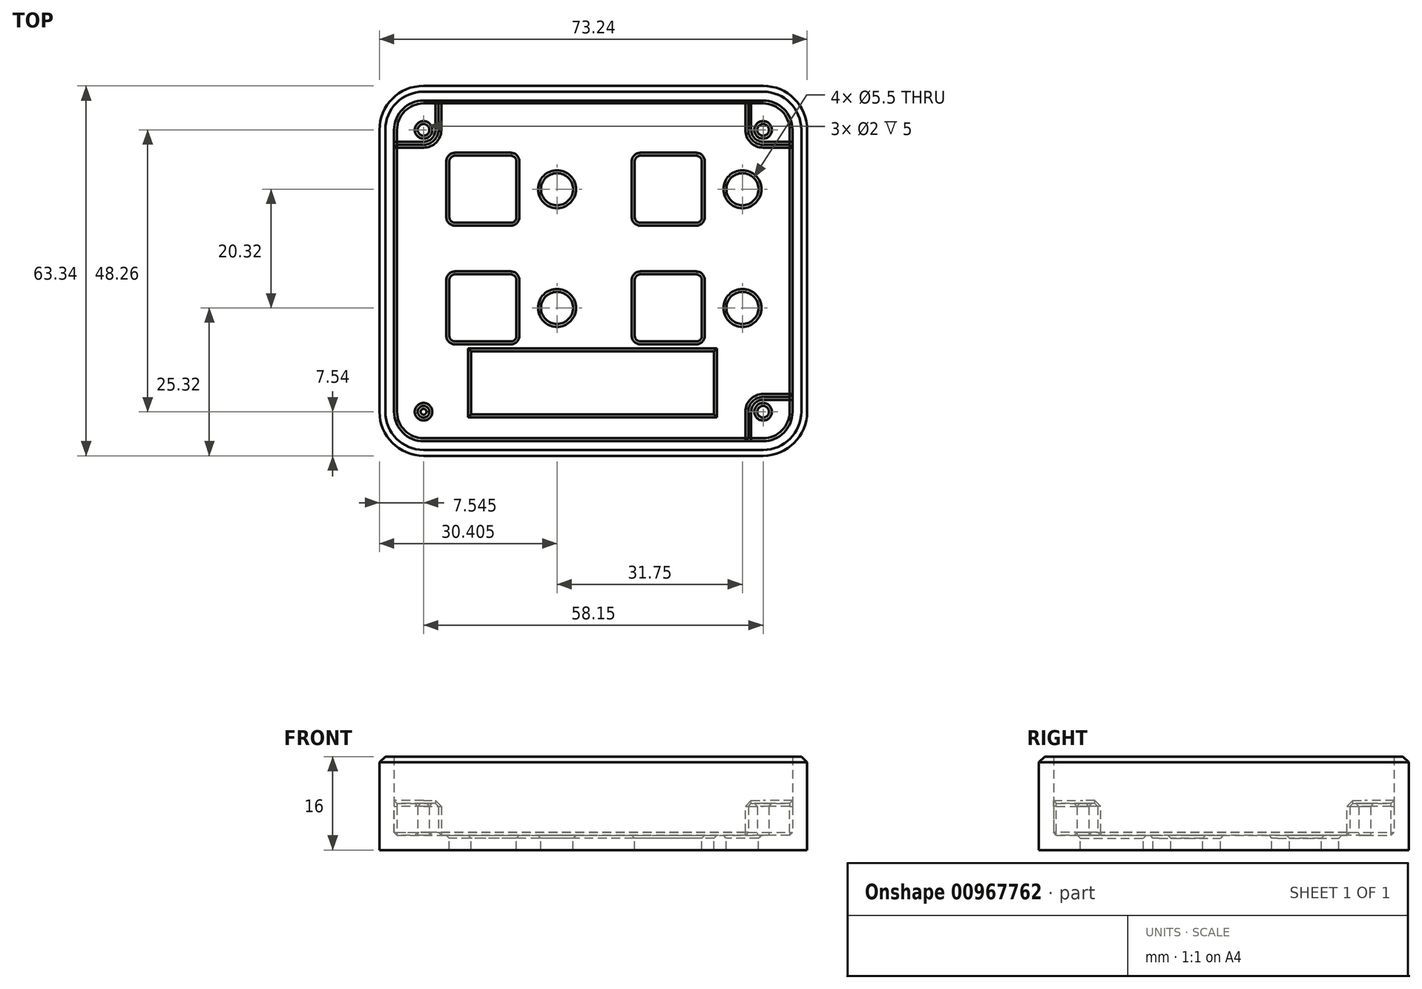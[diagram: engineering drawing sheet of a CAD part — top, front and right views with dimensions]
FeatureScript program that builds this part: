
annotation { "Feature Type Name" : "Feature", "Feature Type Description" : "" }
export const myFeature = defineFeature(function(context is Context, id is Id, definition is map)
    precondition{}
    {
        {
            var Q0;
            Q0=qCreatedBy(makeId("Top.planeOp"),FACE);
            var sketch = newSketch(context, id + "F0", { "sketchPlane" : qUnion([Q0])});
            skLineSegment(sketch, "E0.bottom", {"start": v(36.62, 31.67) * mm, "end": v(-36.61, 31.67) * mm});
            skLineSegment(sketch, "E0.top", {"start": v(36.62, -31.67) * mm, "end": v(-36.62, -31.67) * mm});
            skLineSegment(sketch, "E0.left", {"start": v(36.62, 31.67) * mm, "end": v(36.62, -31.67) * mm});
            skLineSegment(sketch, "E0.right", {"start": v(-36.62, 31.67) * mm, "end": v(-36.62, -31.67) * mm});
            skPoint(sketch, "E0.middle", {"position": v(0, 0) * mm});
            skSolve(sketch);
        }
        {
            var Q0;
            Q0 = qSketchRegion(id + "F0", true);
            extrude(context, id + "F1", {"entities" : qUnion([Q0]), "depth" : 16 * mm, "offsetDistance" : 25 * mm});
        }
        {
            var Q0;
            Q0=makeQuery(id+"F1.opExtrude","SWEPT_EDGE",EDGE,{"disambiguationData":[OSD([sQuery(id+"F0.wireOp",EDGE,"E0.top"),sQuery(id+"F0.wireOp",EDGE,"E0.right")])]});
            var Q1;
            Q1=makeQuery(id+"F1.opExtrude","SWEPT_EDGE",EDGE,{"disambiguationData":[OSD([sQuery(id+"F0.wireOp",EDGE,"E0.top"),sQuery(id+"F0.wireOp",EDGE,"E0.left")])]});
            var Q2;
            Q2=makeQuery(id+"F1.opExtrude","SWEPT_EDGE",EDGE,{"disambiguationData":[OSD([sQuery(id+"F0.wireOp",EDGE,"E0.bottom"),sQuery(id+"F0.wireOp",EDGE,"E0.left")])]});
            var Q3;
            Q3=makeQuery(id+"F1.opExtrude","SWEPT_EDGE",EDGE,{"disambiguationData":[OSD([sQuery(id+"F0.wireOp",EDGE,"E0.bottom"),sQuery(id+"F0.wireOp",EDGE,"E0.right")])]});
            fillet(context, id + "F2", {"entities" : qUnion([Q0, Q1, Q2, Q3]), "radius" : 7.54 * mm, "tangentPropagation" : true, "allowEdgeOverflow" : false});
        }
        {
            var Q0;
            Q0=makeQuery(id+"F1.opExtrude","CAP_FACE",FACE,{"disambiguationData":[OSD([sQuery(id+"F0.wireOp",EDGE,"E0.bottom"),sQuery(id+"F0.wireOp",EDGE,"E0.top"),sQuery(id+"F0.wireOp",EDGE,"E0.left"),sQuery(id+"F0.wireOp",EDGE,"E0.right")])],"isStart":false});
            shell(context, id + "F3", {"entities" : qUnion([Q0]), "thickness" : 2.5 * mm});
        }
        {
            var Q0;
            Q0=makeQuery(id+"F3.opShell","OFFSET_FACE",FACE,{"disambiguationData":[OSD([sQuery(id+"F0.wireOp",EDGE,"E0.bottom"),sQuery(id+"F0.wireOp",EDGE,"E0.top"),sQuery(id+"F0.wireOp",EDGE,"E0.left"),sQuery(id+"F0.wireOp",EDGE,"E0.right")])]});
            var sketch = newSketch(context, id + "F4", { "sketchPlane" : qUnion([Q0])});
            skLineSegment(sketch, "E1", {"start": v(-26.54, 29.17) * mm, "end": v(-26.54, 24.13) * mm});
            skLineSegment(sketch, "E2", {"start": v(-29.08, 21.6) * mm, "end": v(-34.12, 21.6) * mm});
            skCircle(sketch, "E3", {"center": v(-29.08, 24.13) * mm, "radius": 1 * mm});
            skPoint(sketch, "E4.visualSharp", {"position": v(-26.54, 21.6) * mm});
            skArc(sketch, "E4.filletArc", {"start": v(-29.08, 21.6) * mm, "mid": v(-27.28, 22.33) * mm, "end": v(-26.54, 24.13) * mm});
            skLineSegment(sketch, "E5", {"start": v(0, 29.17) * mm, "end": v(0, -29.17) * mm, "construction": true});
            skLineSegment(sketch, "E6", {"start": v(-34.12, 0) * mm, "end": v(34.12, 0) * mm, "construction": true});
            skLineSegment(sketch, "E7.MirrorCS", {"start": v(26.54, 29.17) * mm, "end": v(26.54, 24.13) * mm});
            skLineSegment(sketch, "E8.MirrorCS", {"start": v(29.08, 21.59) * mm, "end": v(34.12, 21.59) * mm});
            skArc(sketch, "E9.MirrorCS", {"start": v(29.08, 21.6) * mm, "mid": v(27.28, 22.33) * mm, "end": v(26.54, 24.13) * mm});
            skCircle(sketch, "E10.MirrorC", {"center": v(29.08, 24.13) * mm, "radius": 1 * mm});
            skCircle(sketch, "E11.MirrorC", {"center": v(-29.08, -24.13) * mm, "radius": 1 * mm});
            skCircle(sketch, "E12.MirrorC", {"center": v(29.07, -24.13) * mm, "radius": 1 * mm});
            skArc(sketch, "E13.MirrorCS", {"start": v(-29.08, -21.59) * mm, "mid": v(-27.28, -22.33) * mm, "end": v(-26.54, -24.13) * mm});
            skLineSegment(sketch, "E14.MirrorCS", {"start": v(-29.08, -21.59) * mm, "end": v(-34.12, -21.59) * mm});
            skLineSegment(sketch, "E15.MirrorCS", {"start": v(26.54, -29.17) * mm, "end": v(26.54, -24.13) * mm});
            skPoint(sketch, "E16.MirrorP", {"position": v(-26.54, -21.59) * mm});
            skLineSegment(sketch, "E17.MirrorCS", {"start": v(-26.54, -29.17) * mm, "end": v(-26.54, -24.13) * mm});
            skLineSegment(sketch, "E18.MirrorCS", {"start": v(29.07, -21.59) * mm, "end": v(34.11, -21.59) * mm});
            skArc(sketch, "E19.MirrorCS", {"start": v(29.07, -21.59) * mm, "mid": v(27.28, -22.33) * mm, "end": v(26.54, -24.13) * mm});
            skSolve(sketch);
        }
        {
            var Q0;
            {var subQ7=sQuery(id+"F4.wireOp",EDGE,"E1");Q0=makeQuery(id+"F4.imprint","IMPRINT",FACE,{"disambiguationData":[TD([[makeQuery(id+"F4.imprint","IMPRINT",EDGE,{"derivedFrom":subQ7}),-1.0]])]});}
            var Q1;
            {var subQ6=sQuery(id+"F4.wireOp",EDGE,"E7.MirrorCS");Q1=makeQuery(id+"F4.imprint","IMPRINT",FACE,{"disambiguationData":[TD([[makeQuery(id+"F4.imprint","IMPRINT",EDGE,{"derivedFrom":subQ6}),1.0]])]});}
            var Q2;
            Q2=makeQuery(id+"F4.imprint","IMPRINT",FACE,{"disambiguationData":[TD([[makeQuery(id+"F4.imprint","IMPRINT",EDGE,{"derivedFrom":sQuery(id+"F4.wireOp",EDGE,"E12.MirrorC")}),-1.0]])]});
            var Q3;
            Q3=makeQuery(id+"F4.imprint","IMPRINT",FACE,{"disambiguationData":[TD([[makeQuery(id+"F4.imprint","IMPRINT",EDGE,{"derivedFrom":sQuery(id+"F4.wireOp",EDGE,"E11.MirrorC")}),1.0]])]});
            extrude(context, id + "F5", {"entities" : qUnion([Q0, Q1, Q2, Q3]), "operationType" : NewBodyOperationType.ADD, "depth" : 5.5 * mm, "offsetDistance" : 25 * mm});
        }
        {
            var Q0;
            {var subQ0=sQuery(id+"F0.wireOp",EDGE,"E0.bottom");var subQ1=sQuery(id+"F0.wireOp",EDGE,"E0.right");var subQ2=sQuery(id+"F0.wireOp",EDGE,"E0.top");var subQ3=sQuery(id+"F0.wireOp",EDGE,"E0.left");Q0=makeQuery(id+"F5.boolean.opBoolean","SPLIT",FACE,{"disambiguationData":[TD([makeQuery(id+"F3.opShell","OFFSET_FACE",FACE,{"disambiguationData":[OSD([subQ0])]})])],"derivedFrom":makeQuery(id+"F3.opShell","OFFSET_FACE",FACE,{"disambiguationData":[OSD([subQ0,subQ2,subQ3,subQ1])]})});}
            var sketch = newSketch(context, id + "F6", { "sketchPlane" : qUnion([Q0])});
            skLineSegment(sketch, "E20.bottom", {"start": v(-14.17, 19.72) * mm, "end": v(-23.67, 19.72) * mm});
            skLineSegment(sketch, "E20.top", {"start": v(-14.17, 8.22) * mm, "end": v(-23.67, 8.22) * mm});
            skLineSegment(sketch, "E20.left", {"start": v(-13.17, 18.72) * mm, "end": v(-13.17, 9.22) * mm});
            skLineSegment(sketch, "E20.right", {"start": v(-24.67, 18.72) * mm, "end": v(-24.67, 9.22) * mm});
            skPoint(sketch, "E20.middle", {"position": v(-18.92, 13.97) * mm});
            skCircle(sketch, "E21", {"center": v(-6.22, 13.97) * mm, "radius": 2.75 * mm});
            skPoint(sketch, "E21.centerSnap0", {"position": v(-13.17, 13.97) * mm});
            skPoint(sketch, "E22.visualSharp", {"position": v(-24.67, 19.72) * mm});
            skArc(sketch, "E22.filletArc", {"start": v(-23.67, 19.72) * mm, "mid": v(-24.37, 19.43) * mm, "end": v(-24.67, 18.72) * mm});
            skPoint(sketch, "E23.visualSharp", {"position": v(-13.17, 19.72) * mm});
            skArc(sketch, "E23.filletArc", {"start": v(-13.17, 18.72) * mm, "mid": v(-13.46, 19.43) * mm, "end": v(-14.17, 19.72) * mm});
            skPoint(sketch, "E24.visualSharp", {"position": v(-13.17, 8.22) * mm});
            skArc(sketch, "E24.filletArc", {"start": v(-14.17, 8.22) * mm, "mid": v(-13.46, 8.51) * mm, "end": v(-13.17, 9.22) * mm});
            skPoint(sketch, "E25.visualSharp", {"position": v(-24.67, 8.22) * mm});
            skArc(sketch, "E25.filletArc", {"start": v(-24.67, 9.22) * mm, "mid": v(-24.37, 8.51) * mm, "end": v(-23.67, 8.22) * mm});
            skPoint(sketch, "E26.1.0.0", {"position": v(12.83, 13.97) * mm});
            skLineSegment(sketch, "E26.1.0.1", {"start": v(17.58, 19.72) * mm, "end": v(8.08, 19.72) * mm});
            skPoint(sketch, "E26.1.0.2", {"position": v(7.08, 8.22) * mm});
            skLineSegment(sketch, "E26.1.0.3", {"start": v(18.58, 18.72) * mm, "end": v(18.58, 9.22) * mm});
            skPoint(sketch, "E26.1.0.4", {"position": v(18.58, 8.22) * mm});
            skPoint(sketch, "E26.1.0.5", {"position": v(18.58, 13.97) * mm});
            skCircle(sketch, "E26.1.0.6", {"center": v(25.54, 13.97) * mm, "radius": 2.75 * mm});
            skPoint(sketch, "E26.1.0.7", {"position": v(7.08, 19.72) * mm});
            skLineSegment(sketch, "E26.1.0.8", {"start": v(7.08, 18.72) * mm, "end": v(7.08, 9.22) * mm});
            skPoint(sketch, "E26.1.0.9", {"position": v(18.58, 19.72) * mm});
            skLineSegment(sketch, "E26.1.0.10", {"start": v(17.58, 8.22) * mm, "end": v(8.08, 8.22) * mm});
            skArc(sketch, "E26.1.0.11", {"start": v(7.08, 9.22) * mm, "mid": v(7.38, 8.51) * mm, "end": v(8.08, 8.22) * mm});
            skArc(sketch, "E26.1.0.12", {"start": v(8.08, 19.72) * mm, "mid": v(7.38, 19.43) * mm, "end": v(7.08, 18.72) * mm});
            skArc(sketch, "E26.1.0.13", {"start": v(17.58, 8.22) * mm, "mid": v(18.3, 8.51) * mm, "end": v(18.58, 9.22) * mm});
            skArc(sketch, "E26.1.0.14", {"start": v(18.58, 18.72) * mm, "mid": v(18.3, 19.43) * mm, "end": v(17.58, 19.72) * mm});
            skLineSegment(sketch, "E26.direction1", {"start": v(-24.67, 8.22) * mm, "end": v(7.08, 8.22) * mm, "construction": true});
            skLineSegment(sketch, "E27.1.0.0", {"start": v(17.59, -12.1) * mm, "end": v(8.08, -12.1) * mm});
            skPoint(sketch, "E27.1.0.1", {"position": v(18.58, -0.6) * mm});
            skPoint(sketch, "E27.1.0.2", {"position": v(-18.91, -6.35) * mm});
            skPoint(sketch, "E27.1.0.3", {"position": v(18.58, -12.1) * mm});
            skLineSegment(sketch, "E27.1.0.4", {"start": v(-24.67, -1.6) * mm, "end": v(-24.67, -11.1) * mm});
            skPoint(sketch, "E27.1.0.5", {"position": v(12.84, -6.35) * mm});
            skPoint(sketch, "E27.1.0.6", {"position": v(-24.67, -12.1) * mm});
            skPoint(sketch, "E27.1.0.7", {"position": v(18.58, -6.35) * mm});
            skLineSegment(sketch, "E27.1.0.8", {"start": v(17.58, -0.6) * mm, "end": v(8.08, -0.6) * mm});
            skCircle(sketch, "E27.1.0.9", {"center": v(25.54, -6.35) * mm, "radius": 2.75 * mm});
            skLineSegment(sketch, "E27.1.0.10", {"start": v(7.08, -1.6) * mm, "end": v(7.08, -11.1) * mm});
            skLineSegment(sketch, "E27.1.0.11", {"start": v(-14.17, -0.6) * mm, "end": v(-23.67, -0.6) * mm});
            skPoint(sketch, "E27.1.0.12", {"position": v(7.08, -0.6) * mm});
            skLineSegment(sketch, "E27.1.0.13", {"start": v(-13.17, -1.6) * mm, "end": v(-13.17, -11.1) * mm});
            skPoint(sketch, "E27.1.0.14", {"position": v(-13.17, -6.35) * mm});
            skPoint(sketch, "E27.1.0.15", {"position": v(-24.67, -0.6) * mm});
            skPoint(sketch, "E27.1.0.16", {"position": v(-13.17, -12.1) * mm});
            skPoint(sketch, "E27.1.0.17", {"position": v(-13.17, -0.6) * mm});
            skLineSegment(sketch, "E27.1.0.18", {"start": v(-24.67, -12.1) * mm, "end": v(7.08, -12.1) * mm, "construction": true});
            skCircle(sketch, "E27.1.0.19", {"center": v(-6.21, -6.35) * mm, "radius": 2.75 * mm});
            skPoint(sketch, "E27.1.0.20", {"position": v(7.08, -12.1) * mm});
            skLineSegment(sketch, "E27.1.0.21", {"start": v(18.58, -1.6) * mm, "end": v(18.58, -11.1) * mm});
            skLineSegment(sketch, "E27.1.0.22", {"start": v(-14.17, -12.1) * mm, "end": v(-23.67, -12.1) * mm});
            skArc(sketch, "E27.1.0.23", {"start": v(8.08, -0.6) * mm, "mid": v(7.38, -0.9) * mm, "end": v(7.08, -1.6) * mm});
            skArc(sketch, "E27.1.0.24", {"start": v(-13.17, -1.6) * mm, "mid": v(-13.46, -0.9) * mm, "end": v(-14.17, -0.6) * mm});
            skArc(sketch, "E27.1.0.25", {"start": v(18.58, -1.6) * mm, "mid": v(18.3, -0.9) * mm, "end": v(17.58, -0.6) * mm});
            skArc(sketch, "E27.1.0.26", {"start": v(17.59, -12.1) * mm, "mid": v(18.3, -11.8) * mm, "end": v(18.59, -11.1) * mm});
            skArc(sketch, "E27.1.0.27", {"start": v(-14.17, -12.1) * mm, "mid": v(-13.46, -11.8) * mm, "end": v(-13.17, -11.1) * mm});
            skArc(sketch, "E27.1.0.28", {"start": v(-23.67, -0.6) * mm, "mid": v(-24.37, -0.9) * mm, "end": v(-24.67, -1.6) * mm});
            skArc(sketch, "E27.1.0.29", {"start": v(-24.67, -11.1) * mm, "mid": v(-24.37, -11.8) * mm, "end": v(-23.67, -12.1) * mm});
            skArc(sketch, "E27.1.0.30", {"start": v(7.08, -11.1) * mm, "mid": v(7.38, -11.8) * mm, "end": v(8.08, -12.1) * mm});
            skLineSegment(sketch, "E27.direction1", {"start": v(-24.67, 8.22) * mm, "end": v(-24.67, -12.1) * mm, "construction": true});
            skLineSegment(sketch, "E28.bottom", {"start": v(20.69, -13.76) * mm, "end": v(-20.95, -13.76) * mm});
            skLineSegment(sketch, "E28.top", {"start": v(20.69, -24.56) * mm, "end": v(-20.95, -24.56) * mm});
            skLineSegment(sketch, "E28.left", {"start": v(20.69, -13.76) * mm, "end": v(20.69, -24.56) * mm});
            skLineSegment(sketch, "E28.right", {"start": v(-20.95, -13.76) * mm, "end": v(-20.95, -24.56) * mm});
            skPoint(sketch, "E28.middle", {"position": v(-0.13, -19.16) * mm});
            skSolve(sketch);
        }
        {
            var Q0;
            Q0=makeQuery(id+"F6.imprint","IMPRINT",FACE,{"disambiguationData":[TD([[makeQuery(id+"F6.imprint","IMPRINT",EDGE,{"derivedFrom":sQuery(id+"F6.wireOp",EDGE,"E20.bottom")}),1.0]])]});
            var Q1;
            Q1=makeQuery(id+"F6.imprint","IMPRINT",FACE,{"disambiguationData":[TD([[makeQuery(id+"F6.imprint","IMPRINT",EDGE,{"derivedFrom":sQuery(id+"F6.wireOp",EDGE,"E21")}),1.0]])]});
            var Q2;
            Q2=makeQuery(id+"F6.imprint","IMPRINT",FACE,{"disambiguationData":[TD([[makeQuery(id+"F6.imprint","IMPRINT",EDGE,{"derivedFrom":sQuery(id+"F6.wireOp",EDGE,"E26.1.0.1")}),1.0]])]});
            var Q3;
            Q3=makeQuery(id+"F6.imprint","IMPRINT",FACE,{"disambiguationData":[TD([[makeQuery(id+"F6.imprint","IMPRINT",EDGE,{"derivedFrom":sQuery(id+"F6.wireOp",EDGE,"E26.1.0.6")}),1.0]])]});
            var Q4;
            Q4=makeQuery(id+"F6.imprint","IMPRINT",FACE,{"disambiguationData":[TD([[makeQuery(id+"F6.imprint","IMPRINT",EDGE,{"derivedFrom":sQuery(id+"F6.wireOp",EDGE,"E27.1.0.4")}),1.0]])]});
            var Q5;
            Q5=makeQuery(id+"F6.imprint","IMPRINT",FACE,{"disambiguationData":[TD([[makeQuery(id+"F6.imprint","IMPRINT",EDGE,{"derivedFrom":sQuery(id+"F6.wireOp",EDGE,"E27.1.0.19")}),1.0]])]});
            var Q6;
            Q6=makeQuery(id+"F6.imprint","IMPRINT",FACE,{"disambiguationData":[TD([[makeQuery(id+"F6.imprint","IMPRINT",EDGE,{"derivedFrom":sQuery(id+"F6.wireOp",EDGE,"E27.1.0.0")}),-1.0]])]});
            var Q7;
            Q7=makeQuery(id+"F6.imprint","IMPRINT",FACE,{"disambiguationData":[TD([[makeQuery(id+"F6.imprint","IMPRINT",EDGE,{"derivedFrom":sQuery(id+"F6.wireOp",EDGE,"E27.1.0.9")}),1.0]])]});
            var Q8;
            Q8=makeQuery(id+"F6.imprint","IMPRINT",FACE,{"disambiguationData":[TD([[makeQuery(id+"F6.imprint","IMPRINT",EDGE,{"derivedFrom":sQuery(id+"F6.wireOp",EDGE,"E28.bottom")}),1.0]])]});
            extrude(context, id + "F7", {"entities" : qUnion([Q0, Q1, Q2, Q3, Q4, Q5, Q6, Q7, Q8]), "operationType" : NewBodyOperationType.REMOVE, "endBound" : BoundingType.UP_TO_NEXT, "oppositeDirection" : true, "depth" : 25 * mm, "offsetDistance" : 25 * mm});
        }
        {
            var Q0;
            {var subQ0=sQuery(id+"F0.wireOp",EDGE,"E0.bottom");var subQ1=sQuery(id+"F0.wireOp",EDGE,"E0.left");var subQ2=sQuery(id+"F0.wireOp",EDGE,"E0.top");var subQ3=sQuery(id+"F0.wireOp",EDGE,"E0.right");Q0=makeQuery(id+"F5.boolean.opBoolean","SPLIT",FACE,{"disambiguationData":[TD([makeQuery(id+"F3.opShell","OFFSET_FACE",FACE,{"disambiguationData":[OSD([subQ0])]})])],"derivedFrom":makeQuery(id+"F3.opShell","OFFSET_FACE",FACE,{"disambiguationData":[OSD([subQ0,subQ2,subQ1,subQ3])]})});}
            var Q1;
            Q1=makeQuery(id+"F5.opExtrude","CAP_FACE",FACE,{"disambiguationData":[OSD([sQuery(id+"F0.wireOp",EDGE,"E0.bottom"),sQuery(id+"F0.wireOp",EDGE,"E0.top"),sQuery(id+"F0.wireOp",EDGE,"E0.left"),sQuery(id+"F0.wireOp",EDGE,"E0.right"),sQuery(id+"F4.wireOp",EDGE,"E1"),sQuery(id+"F4.wireOp",EDGE,"E2"),sQuery(id+"F4.wireOp",EDGE,"E3"),sQuery(id+"F4.wireOp",EDGE,"E4.filletArc")])],"isStart":false});
            var Q2;
            Q2=makeQuery(id+"F5.opExtrude","CAP_FACE",FACE,{"disambiguationData":[OSD([sQuery(id+"F0.wireOp",EDGE,"E0.bottom"),sQuery(id+"F0.wireOp",EDGE,"E0.top"),sQuery(id+"F0.wireOp",EDGE,"E0.left"),sQuery(id+"F0.wireOp",EDGE,"E0.right"),sQuery(id+"F4.wireOp",EDGE,"E7.MirrorCS"),sQuery(id+"F4.wireOp",EDGE,"E8.MirrorCS"),sQuery(id+"F4.wireOp",EDGE,"E9.MirrorCS"),sQuery(id+"F4.wireOp",EDGE,"E10.MirrorC")])],"isStart":false});
            var Q3;
            Q3=makeQuery(id+"F5.opExtrude","CAP_FACE",FACE,{"disambiguationData":[OSD([sQuery(id+"F0.wireOp",EDGE,"E0.bottom"),sQuery(id+"F0.wireOp",EDGE,"E0.top"),sQuery(id+"F0.wireOp",EDGE,"E0.left"),sQuery(id+"F0.wireOp",EDGE,"E0.right"),sQuery(id+"F4.wireOp",EDGE,"E12.MirrorC"),sQuery(id+"F4.wireOp",EDGE,"E15.MirrorCS"),sQuery(id+"F4.wireOp",EDGE,"E18.MirrorCS"),sQuery(id+"F4.wireOp",EDGE,"E19.MirrorCS")])],"isStart":false});
            var Q4;
            Q4=makeQuery(id+"F5.opExtrude","CAP_FACE",FACE,{"disambiguationData":[OSD([sQuery(id+"F0.wireOp",EDGE,"E0.bottom"),sQuery(id+"F0.wireOp",EDGE,"E0.top"),sQuery(id+"F0.wireOp",EDGE,"E0.left"),sQuery(id+"F0.wireOp",EDGE,"E0.right"),sQuery(id+"F4.wireOp",EDGE,"E11.MirrorC"),sQuery(id+"F4.wireOp",EDGE,"E13.MirrorCS"),sQuery(id+"F4.wireOp",EDGE,"E14.MirrorCS"),sQuery(id+"F4.wireOp",EDGE,"E17.MirrorCS")])],"isStart":false});
            chamfer(context, id + "F8", {"entities" : qUnion([Q0, Q1, Q2, Q3, Q4]), "width" : .5 * mm, "tangentPropagation" : true});
        }
        {
            var Q0;
            Q0=makeQuery(id+"F1.opExtrude","CAP_EDGE",EDGE,{"disambiguationData":[OSD([sQuery(id+"F0.wireOp",EDGE,"E0.left")])],"isStart":false});
            var Q1;
            {var subQ0=sQuery(id+"F0.wireOp",EDGE,"E0.left");var subQ1=sQuery(id+"F0.wireOp",EDGE,"E0.bottom");Q1=makeQuery(id+"F2.opFillet","BLEND_EDGE",EDGE,{"blendedFrom":[makeQuery(id+"F1.opExtrude","SWEPT_EDGE",EDGE,{"disambiguationData":[OSD([subQ1,subQ0])]}),makeQuery(id+"F1.opExtrude","CAP_FACE",FACE,{"disambiguationData":[OSD([subQ1,sQuery(id+"F0.wireOp",EDGE,"E0.top"),subQ0,sQuery(id+"F0.wireOp",EDGE,"E0.right")])],"isStart":false})],"blendedInto":[makeQuery(id+"F1.opExtrude","CAP_FACE",FACE,{"disambiguationData":[OSD([subQ1,sQuery(id+"F0.wireOp",EDGE,"E0.top"),subQ0,sQuery(id+"F0.wireOp",EDGE,"E0.right")])],"isStart":false})]});}
            var Q2;
            Q2=makeQuery(id+"F1.opExtrude","CAP_EDGE",EDGE,{"disambiguationData":[OSD([sQuery(id+"F0.wireOp",EDGE,"E0.bottom")])],"isStart":false});
            var Q3;
            {var subQ0=sQuery(id+"F0.wireOp",EDGE,"E0.right");var subQ1=sQuery(id+"F0.wireOp",EDGE,"E0.bottom");Q3=makeQuery(id+"F2.opFillet","BLEND_EDGE",EDGE,{"blendedFrom":[makeQuery(id+"F1.opExtrude","SWEPT_EDGE",EDGE,{"disambiguationData":[OSD([subQ1,subQ0])]}),makeQuery(id+"F1.opExtrude","CAP_FACE",FACE,{"disambiguationData":[OSD([subQ1,sQuery(id+"F0.wireOp",EDGE,"E0.top"),sQuery(id+"F0.wireOp",EDGE,"E0.left"),subQ0])],"isStart":false})],"blendedInto":[makeQuery(id+"F1.opExtrude","CAP_FACE",FACE,{"disambiguationData":[OSD([subQ1,sQuery(id+"F0.wireOp",EDGE,"E0.top"),sQuery(id+"F0.wireOp",EDGE,"E0.left"),subQ0])],"isStart":false})]});}
            var Q4;
            Q4=makeQuery(id+"F1.opExtrude","CAP_EDGE",EDGE,{"disambiguationData":[OSD([sQuery(id+"F0.wireOp",EDGE,"E0.right")])],"isStart":false});
            var Q5;
            {var subQ0=sQuery(id+"F0.wireOp",EDGE,"E0.left");var subQ1=sQuery(id+"F0.wireOp",EDGE,"E0.top");Q5=makeQuery(id+"F2.opFillet","BLEND_EDGE",EDGE,{"blendedFrom":[makeQuery(id+"F1.opExtrude","SWEPT_EDGE",EDGE,{"disambiguationData":[OSD([subQ1,subQ0])]}),makeQuery(id+"F1.opExtrude","CAP_FACE",FACE,{"disambiguationData":[OSD([sQuery(id+"F0.wireOp",EDGE,"E0.bottom"),subQ1,subQ0,sQuery(id+"F0.wireOp",EDGE,"E0.right")])],"isStart":false})],"blendedInto":[makeQuery(id+"F1.opExtrude","CAP_FACE",FACE,{"disambiguationData":[OSD([sQuery(id+"F0.wireOp",EDGE,"E0.bottom"),subQ1,subQ0,sQuery(id+"F0.wireOp",EDGE,"E0.right")])],"isStart":false})]});}
            var Q6;
            {var subQ0=sQuery(id+"F0.wireOp",EDGE,"E0.right");var subQ1=sQuery(id+"F0.wireOp",EDGE,"E0.top");Q6=makeQuery(id+"F2.opFillet","BLEND_EDGE",EDGE,{"blendedFrom":[makeQuery(id+"F1.opExtrude","SWEPT_EDGE",EDGE,{"disambiguationData":[OSD([subQ1,subQ0])]}),makeQuery(id+"F1.opExtrude","CAP_FACE",FACE,{"disambiguationData":[OSD([sQuery(id+"F0.wireOp",EDGE,"E0.bottom"),subQ1,sQuery(id+"F0.wireOp",EDGE,"E0.left"),subQ0])],"isStart":false})],"blendedInto":[makeQuery(id+"F1.opExtrude","CAP_FACE",FACE,{"disambiguationData":[OSD([sQuery(id+"F0.wireOp",EDGE,"E0.bottom"),subQ1,sQuery(id+"F0.wireOp",EDGE,"E0.left"),subQ0])],"isStart":false})]});}
            chamfer(context, id + "F9", {"entities" : qUnion([Q0, Q1, Q2, Q3, Q4, Q5, Q6]), "width" : mm, "tangentPropagation" : true});
        }
    });
